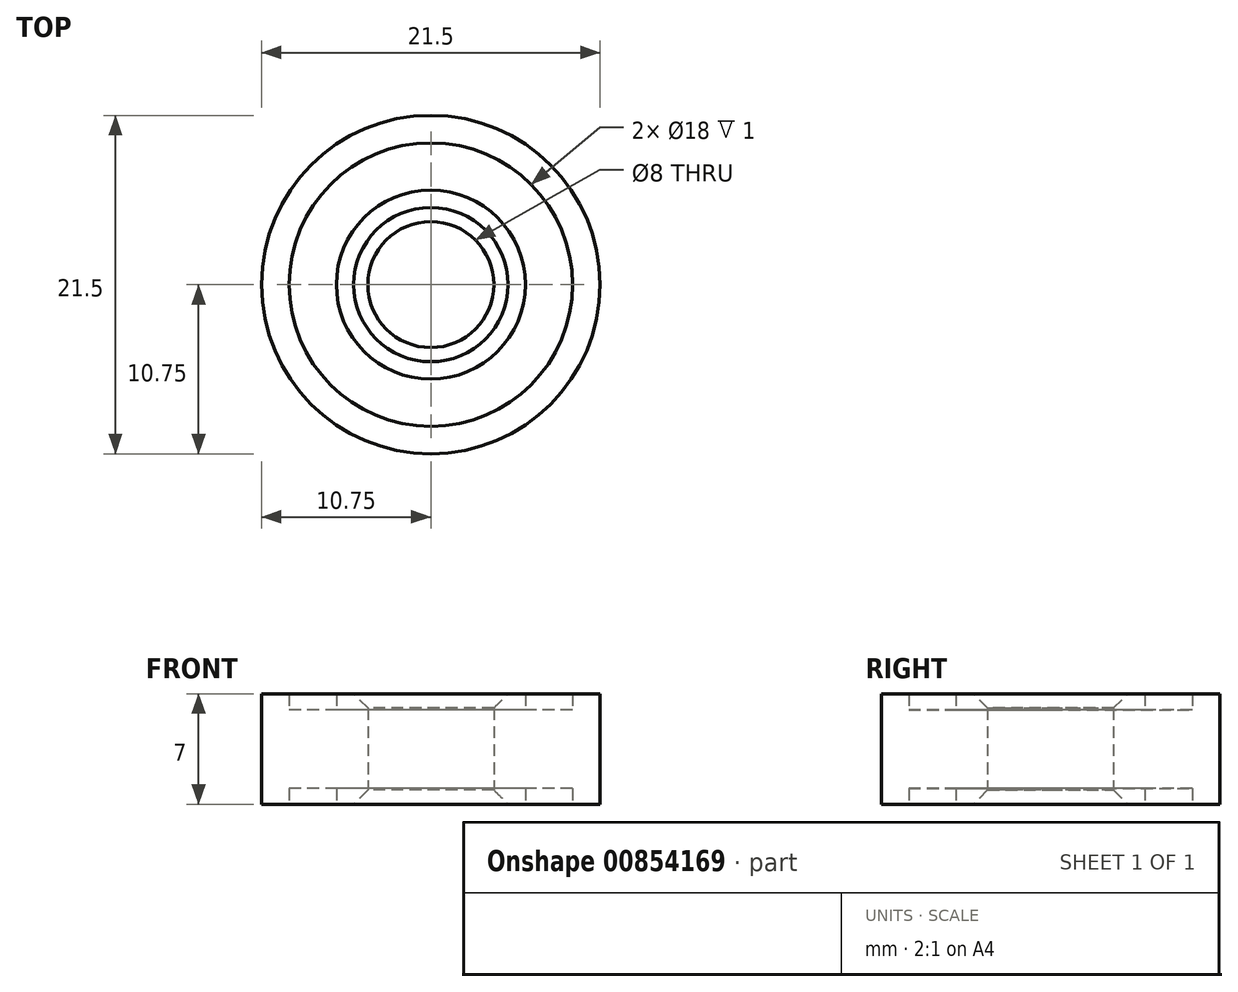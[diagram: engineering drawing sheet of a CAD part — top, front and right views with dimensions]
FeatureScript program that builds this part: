
annotation { "Feature Type Name" : "Feature", "Feature Type Description" : "" }
export const myFeature = defineFeature(function(context is Context, id is Id, definition is map)
    precondition{}
    {
        {
            var Q0;
            Q0=qCreatedBy(makeId("Top.planeOp"),FACE);
            var sketch = newSketch(context, id + "F0", { "sketchPlane" : qUnion([Q0])});
            skCircle(sketch, "E0", {"center": v(0, 0) * mm, "radius": 10.75 * mm});
            skCircle(sketch, "E1", {"center": v(0, 0) * mm, "radius": 4 * mm});
            skCircle(sketch, "E2", {"center": v(0, 0) * mm, "radius": 6 * mm});
            skCircle(sketch, "E3", {"center": v(0, 0) * mm, "radius": 9 * mm});
            skSolve(sketch);
        }
        {
            var Q0;
            Q0=makeQuery(id+"F0.imprint","IMPRINT",FACE,{"disambiguationData":[TD([[makeQuery(id+"F0.imprint","IMPRINT",EDGE,{"derivedFrom":sQuery(id+"F0.wireOp",EDGE,"E2")}),-1.0]])]});
            extrude(context, id + "F1", {"entities" : qUnion([Q0]), "endBound" : BoundingType.SYMMETRIC, "depth" : 5 * mm, "offsetDistance" : 25 * mm});
        }
        {
            var Q0;
            Q0=makeQuery(id+"F0.imprint","IMPRINT",FACE,{"disambiguationData":[TD([[makeQuery(id+"F0.imprint","IMPRINT",EDGE,{"derivedFrom":sQuery(id+"F0.wireOp",EDGE,"E0")}),1.0]])]});
            var Q1;
            Q1=makeQuery(id+"F0.imprint","IMPRINT",FACE,{"disambiguationData":[TD([[makeQuery(id+"F0.imprint","IMPRINT",EDGE,{"derivedFrom":sQuery(id+"F0.wireOp",EDGE,"E1")}),-1.0]])]});
            extrude(context, id + "F2", {"entities" : qUnion([Q0, Q1]), "operationType" : NewBodyOperationType.ADD, "endBound" : BoundingType.SYMMETRIC, "depth" : 7 * mm, "offsetDistance" : 25 * mm});
        }
        {
            var Q0;
            Q0=makeQuery(id+"F1.opExtrude","SWEPT_BODY",BODY,{"disambiguationData":[OSD([sQuery(id+"F0.wireOp",EDGE,"E2"),sQuery(id+"F0.wireOp",EDGE,"E3")])]});
            transform(context, id + "F3", {"entities" : qUnion([Q0]), "transformType" : TransformType.TRANSLATION_3D, "dx" : 0 * mm, "dy" : 0 * mm, "dz" : 4.5 * mm, "makeCopy" : false});
        }
        {
            var Q0;
            Q0=makeQuery(id+"F2.opExtrude","CAP_EDGE",EDGE,{"disambiguationData":[OSD([sQuery(id+"F0.wireOp",EDGE,"E1")])],"isStart":false});
            var Q1;
            Q1=makeQuery(id+"F2.opExtrude","CAP_EDGE",EDGE,{"disambiguationData":[OSD([sQuery(id+"F0.wireOp",EDGE,"E1")])],"isStart":true});
            chamfer(context, id + "F4", {"entities" : qUnion([Q0, Q1]), "width" : 0.9 * mm, "tangentPropagation" : true});
        }
        {
            var Q0;
            Q0=makeQuery(id+"F1.opExtrude","SWEPT_BODY",BODY,{"disambiguationData":[OSD([sQuery(id+"F0.wireOp",EDGE,"E2"),sQuery(id+"F0.wireOp",EDGE,"E3")])]});
            transform(context, id + "F5", {"entities" : qUnion([Q0]), "transformType" : TransformType.TRANSLATION_3D, "dx" : 0 * mm, "dy" : 0 * mm, "dz" : 2.5 * mm, "makeCopy" : false});
        }
    });
